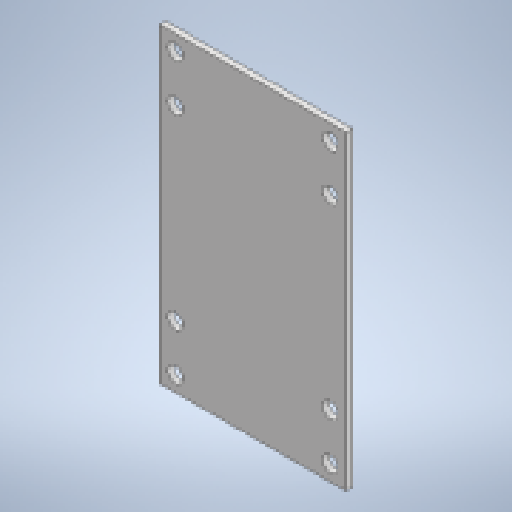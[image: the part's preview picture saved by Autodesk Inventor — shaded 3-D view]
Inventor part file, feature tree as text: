
AUTODESK INVENTOR PART (.ipt)
format: ipt  version: 2025 (Build 290162010, 162A)  size: 249,344 bytes
history: native  units: mm
features: sketch x2, sheet_metal_op x1, hole x1, mirror x1, other x1, projected_geometry x1
ambient origin geometry x8: Origin, YZ Plane, XZ Plane, XY Plane, X Axis, Y Axis, Z Axis, Center Point
bodies: Solid1 (feature_tree)
feature tree (7):
  sheet_metal_op  "Face1"
  hole  "Hole1"  [1 undecoded]
  mirror  "Mirror1"
  sketch  "Sketch1"  dims[d2=8.0mm]
  other  "Plate1"
  sketch  "Sketch2"  dims[d3=20.0mm d4=6.0mm d5=4.0mm d6=2.0mm d7=90.0deg d8=8.0mm d9=20.594885mm d16=240.0mm d17=400.0mm d19=20.0mm d20=20.0mm d21=360.0mm d22=120.0mm d23=120.0mm]
  projected_geometry  "Projected Loop1"
note: 1 required parameter value undecoded (feature->parameter linkage not recoverable at this tier; creation-order binding heuristic only, values carry confidence <= 0.55)
